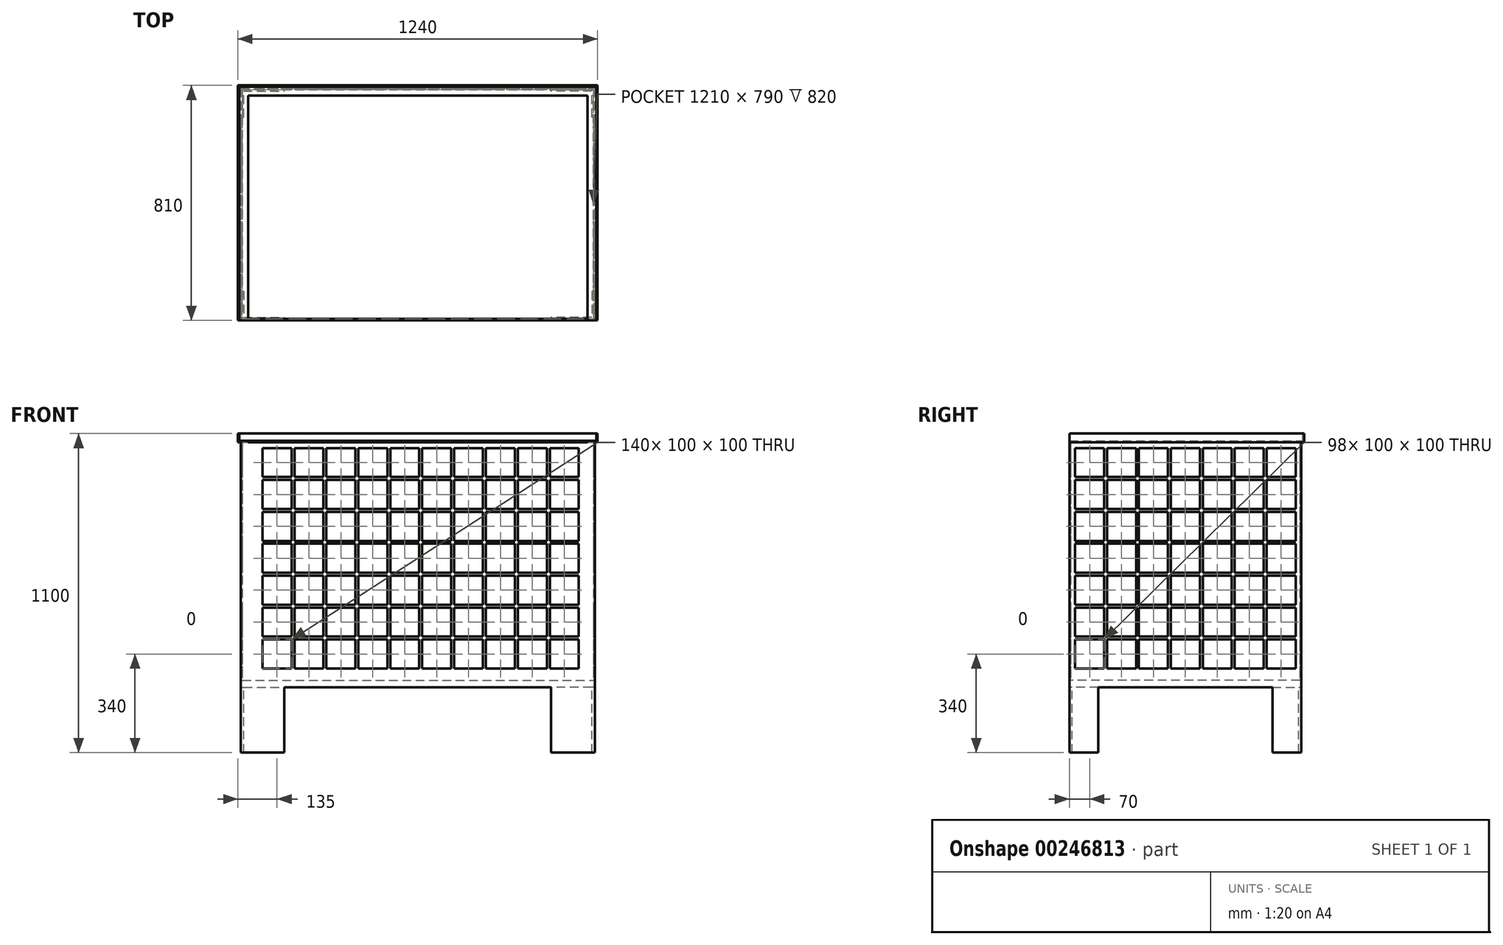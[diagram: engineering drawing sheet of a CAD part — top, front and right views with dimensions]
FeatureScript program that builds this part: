
annotation { "Feature Type Name" : "Feature", "Feature Type Description" : "" }
export const myFeature = defineFeature(function(context is Context, id is Id, definition is map)
    precondition{}
    {
        {
            var Q0;
            Q0=qCreatedBy(makeId("Top.planeOp"),FACE);
            var sketch = newSketch(context, id + "F0", { "sketchPlane" : qUnion([Q0])});
            skLineSegment(sketch, "E0.bottom", {"start": v(-610, 400) * mm, "end": v(610, 400) * mm});
            skLineSegment(sketch, "E0.top", {"start": v(-610, -400) * mm, "end": v(610, -400) * mm});
            skLineSegment(sketch, "E0.left", {"start": v(-610, 400) * mm, "end": v(-610, -400) * mm});
            skLineSegment(sketch, "E0.right", {"start": v(610, 400) * mm, "end": v(610, -400) * mm});
            skPoint(sketch, "E0.middle", {"position": v(0, 0) * mm});
            skSolve(sketch);
        }
        {
            var Q0;
            Q0=makeQuery(id+"F0.imprint","IMPRINT",FACE,{"disambiguationData":[TD([[makeQuery(id+"F0.imprint","IMPRINT",EDGE,{"derivedFrom":sQuery(id+"F0.wireOp",EDGE,"E0.bottom")}),-1.0]])]});
            extrude(context, id + "F1", {"entities" : qUnion([Q0]), "depth" : 25 * mm});
        }
        {
            var Q0;
            Q0=makeQuery(id+"F1.opExtrude","CAP_FACE",FACE,{"disambiguationData":[OSD([sQuery(id+"F0.wireOp",EDGE,"E0.bottom"),sQuery(id+"F0.wireOp",EDGE,"E0.top"),sQuery(id+"F0.wireOp",EDGE,"E0.left"),sQuery(id+"F0.wireOp",EDGE,"E0.right")])],"isStart":true});
            var sketch = newSketch(context, id + "F2", { "sketchPlane" : qUnion([Q0])});
            skLineSegment(sketch, "E1", {"start": v(-610, 400) * mm, "end": v(-610, 300) * mm});
            skLineSegment(sketch, "E2", {"start": v(-610, 300) * mm, "end": v(-600, 300) * mm});
            skLineSegment(sketch, "E3", {"start": v(-600, 300) * mm, "end": v(-600, 390) * mm});
            skLineSegment(sketch, "E4", {"start": v(-600, 390) * mm, "end": v(-460, 390) * mm});
            skLineSegment(sketch, "E5", {"start": v(-460, 390) * mm, "end": v(-460, 400) * mm});
            skLineSegment(sketch, "E6", {"start": v(-460, 400) * mm, "end": v(-610, 400) * mm});
            skLineSegment(sketch, "E7.MirrorCS", {"start": v(460, 390) * mm, "end": v(460, 400) * mm});
            skLineSegment(sketch, "E8.MirrorCS", {"start": v(610, 300) * mm, "end": v(600, 300) * mm});
            skLineSegment(sketch, "E9.MirrorCS", {"start": v(460, 400) * mm, "end": v(610, 400) * mm});
            skLineSegment(sketch, "E10.MirrorCS", {"start": v(600, 390) * mm, "end": v(460, 390) * mm});
            skLineSegment(sketch, "E11.MirrorCS", {"start": v(600, 300) * mm, "end": v(600, 390) * mm});
            skLineSegment(sketch, "E12.MirrorCS", {"start": v(610, 400) * mm, "end": v(610, 300) * mm});
            skLineSegment(sketch, "E13.MirrorCS", {"start": v(-610, -300) * mm, "end": v(-600, -300) * mm});
            skLineSegment(sketch, "E14.MirrorCS", {"start": v(460, -390) * mm, "end": v(460, -400) * mm});
            skLineSegment(sketch, "E15.MirrorCS", {"start": v(610, -300) * mm, "end": v(600, -300) * mm});
            skLineSegment(sketch, "E16.MirrorCS", {"start": v(-460, -390) * mm, "end": v(-460, -400) * mm});
            skLineSegment(sketch, "E17.MirrorCS", {"start": v(460, -400) * mm, "end": v(610, -400) * mm});
            skLineSegment(sketch, "E18.MirrorCS", {"start": v(600, -390) * mm, "end": v(460, -390) * mm});
            skLineSegment(sketch, "E19.MirrorCS", {"start": v(600, -300) * mm, "end": v(600, -390) * mm});
            skLineSegment(sketch, "E20.MirrorCS", {"start": v(610, -400) * mm, "end": v(610, -300) * mm});
            skLineSegment(sketch, "E21.MirrorCS", {"start": v(-460, -400) * mm, "end": v(-610, -400) * mm});
            skLineSegment(sketch, "E22.MirrorCS", {"start": v(-600, -300) * mm, "end": v(-600, -390) * mm});
            skLineSegment(sketch, "E23.MirrorCS", {"start": v(-600, -390) * mm, "end": v(-460, -390) * mm});
            skLineSegment(sketch, "E24.MirrorCS", {"start": v(-610, -400) * mm, "end": v(-610, -300) * mm});
            skSolve(sketch);
        }
        {
            var Q0;
            Q0 = qSketchRegion(id + "F2", true);
            extrude(context, id + "F3", {"entities" : qUnion([Q0]), "operationType" : NewBodyOperationType.ADD, "depth" : 225 * mm});
        }
        {
            var Q0;
            Q0=makeQuery(id+"F1.opExtrude","CAP_FACE",FACE,{"disambiguationData":[OSD([sQuery(id+"F0.wireOp",EDGE,"E0.bottom"),sQuery(id+"F0.wireOp",EDGE,"E0.top"),sQuery(id+"F0.wireOp",EDGE,"E0.left"),sQuery(id+"F0.wireOp",EDGE,"E0.right")])],"isStart":false});
            var sketch = newSketch(context, id + "F4", { "sketchPlane" : qUnion([Q0])});
            skLineSegment(sketch, "E25.0", {"start": v(-610, 400) * mm, "end": v(-610, -400) * mm});
            skLineSegment(sketch, "E26.0", {"start": v(-610, 400) * mm, "end": v(610, 400) * mm});
            skLineSegment(sketch, "E27.0", {"start": v(610, 400) * mm, "end": v(610, -400) * mm});
            skLineSegment(sketch, "E28.0", {"start": v(-610, -400) * mm, "end": v(610, -400) * mm});
            skLineSegment(sketch, "E29.0", {"start": v(-605, 395) * mm, "end": v(-605, -395) * mm});
            skLineSegment(sketch, "E29.1", {"start": v(-605, 395) * mm, "end": v(605, 395) * mm});
            skLineSegment(sketch, "E29.2", {"start": v(605, 395) * mm, "end": v(605, -395) * mm});
            skLineSegment(sketch, "E29.3", {"start": v(-605, -395) * mm, "end": v(605, -395) * mm});
            skSolve(sketch);
        }
        {
            var Q0;
            Q0 = qSketchRegion(id + "F4", true);
            extrude(context, id + "F5", {"entities" : qUnion([Q0]), "operationType" : NewBodyOperationType.ADD, "depth" : 820 * mm});
        }
        {
            var Q0;
            Q0=makeQuery(id+"F5.boolean.opBoolean","MERGE",FACE,{"derivedFrom":[makeQuery(id+"F3.boolean.opBoolean","MERGE",FACE,{"derivedFrom":[makeQuery(id+"F1.opExtrude","SWEPT_FACE",FACE,{"disambiguationData":[OSD([sQuery(id+"F0.wireOp",EDGE,"E0.top")])]}),makeQuery(id+"F3.opExtrude","SWEPT_FACE",FACE,{"disambiguationData":[OSD([sQuery(id+"F2.wireOp",EDGE,"E9.MirrorCS")])]}),makeQuery(id+"F3.opExtrude","SWEPT_FACE",FACE,{"disambiguationData":[OSD([sQuery(id+"F2.wireOp",EDGE,"E6")])]})]}),makeQuery(id+"F5.opExtrude","SWEPT_FACE",FACE,{"disambiguationData":[OSD([sQuery(id+"F4.wireOp",EDGE,"E28.0")])]})]});
            var sketch = newSketch(context, id + "F6", { "sketchPlane" : qUnion([Q0])});
            skLineSegment(sketch, "E30", {"start": v(-585, 845) * mm, "end": v(-620, 845) * mm});
            skLineSegment(sketch, "E31", {"start": v(-620, 845) * mm, "end": v(-620, 875) * mm});
            skLineSegment(sketch, "E32", {"start": v(-620, 875) * mm, "end": v(-615, 875) * mm});
            skLineSegment(sketch, "E33", {"start": v(-615, 875) * mm, "end": v(-615, 850) * mm});
            skLineSegment(sketch, "E34", {"start": v(-615, 850) * mm, "end": v(-585, 850) * mm});
            skLineSegment(sketch, "E35", {"start": v(-585, 850) * mm, "end": v(-585, 845) * mm});
            skSolve(sketch);
        }
        {
            var Q0;
            Q0=makeQuery(id+"F5.opExtrude","CAP_FACE",FACE,{"disambiguationData":[OSD([sQuery(id+"F4.wireOp",EDGE,"E25.0"),sQuery(id+"F4.wireOp",EDGE,"E26.0"),sQuery(id+"F4.wireOp",EDGE,"E27.0"),sQuery(id+"F4.wireOp",EDGE,"E28.0"),sQuery(id+"F4.wireOp",EDGE,"E29.0"),sQuery(id+"F4.wireOp",EDGE,"E29.1"),sQuery(id+"F4.wireOp",EDGE,"E29.2"),sQuery(id+"F4.wireOp",EDGE,"E29.3")])],"isStart":false});
            var sketch = newSketch(context, id + "F7", { "sketchPlane" : qUnion([Q0])});
            skLineSegment(sketch, "E36.0", {"start": v(-610, 400) * mm, "end": v(-610, -400) * mm});
            skLineSegment(sketch, "E37.0", {"start": v(-610, 400) * mm, "end": v(610, 400) * mm});
            skLineSegment(sketch, "E38.0", {"start": v(610, 400) * mm, "end": v(610, -400) * mm});
            skSolve(sketch);
        }
        {
            var Q0;
            {var subQ0=sQuery(id+"F6.wireOp",EDGE,"E31");Q0=makeQuery(id+"F6.imprint","IMPRINT",FACE,{"disambiguationData":[TD([[makeQuery(id+"F6.imprint","IMPRINT",EDGE,{"derivedFrom":subQ0}),-1.0]])]});}
            var Q1;
            Q1 = qConstructionFilter(qBodyType(qCreatedBy(id + "F7" ,EDGE), BodyType.WIRE), ConstructionObject.NO);
            sweep(context, id + "F8", {"operationType" : NewBodyOperationType.ADD, "profiles" : qUnion([Q0]), "path" : qUnion([Q1])});
        }
        {
            var Q0;
            Q0=makeQuery(id+"F5.boolean.opBoolean","MERGE",FACE,{"derivedFrom":[makeQuery(id+"F3.boolean.opBoolean","MERGE",FACE,{"derivedFrom":[makeQuery(id+"F1.opExtrude","SWEPT_FACE",FACE,{"disambiguationData":[OSD([sQuery(id+"F0.wireOp",EDGE,"E0.right")])]}),makeQuery(id+"F3.opExtrude","SWEPT_FACE",FACE,{"disambiguationData":[OSD([sQuery(id+"F2.wireOp",EDGE,"E12.MirrorCS")])]}),makeQuery(id+"F3.opExtrude","SWEPT_FACE",FACE,{"disambiguationData":[OSD([sQuery(id+"F2.wireOp",EDGE,"E20.MirrorCS")])]})]}),makeQuery(id+"F5.opExtrude","SWEPT_FACE",FACE,{"disambiguationData":[OSD([sQuery(id+"F4.wireOp",EDGE,"E27.0")])]})]});
            var sketch = newSketch(context, id + "F9", { "sketchPlane" : qUnion([Q0])});
            skLineSegment(sketch, "E39.bottom", {"start": v(-380, 825) * mm, "end": v(-280, 825) * mm});
            skLineSegment(sketch, "E39.top", {"start": v(-380, 725) * mm, "end": v(-280, 725) * mm});
            skLineSegment(sketch, "E39.left", {"start": v(-380, 825) * mm, "end": v(-380, 725) * mm});
            skLineSegment(sketch, "E39.right", {"start": v(-280, 825) * mm, "end": v(-280, 725) * mm});
            skLineSegment(sketch, "E40.0.1.0", {"start": v(-380, 715) * mm, "end": v(-280, 715) * mm});
            skLineSegment(sketch, "E40.0.1.1", {"start": v(-380, 715) * mm, "end": v(-380, 615) * mm});
            skLineSegment(sketch, "E40.0.1.2", {"start": v(-280, 715) * mm, "end": v(-280, 615) * mm});
            skLineSegment(sketch, "E40.0.1.3", {"start": v(-380, 615) * mm, "end": v(-280, 615) * mm});
            skLineSegment(sketch, "E40.0.2.0", {"start": v(-380, 605) * mm, "end": v(-280, 605) * mm});
            skLineSegment(sketch, "E40.0.2.1", {"start": v(-380, 605) * mm, "end": v(-380, 505) * mm});
            skLineSegment(sketch, "E40.0.2.2", {"start": v(-280, 605) * mm, "end": v(-280, 505) * mm});
            skLineSegment(sketch, "E40.0.2.3", {"start": v(-380, 505) * mm, "end": v(-280, 505) * mm});
            skLineSegment(sketch, "E40.0.3.0", {"start": v(-380, 495) * mm, "end": v(-280, 495) * mm});
            skLineSegment(sketch, "E40.0.3.1", {"start": v(-380, 495) * mm, "end": v(-380, 395) * mm});
            skLineSegment(sketch, "E40.0.3.2", {"start": v(-280, 495) * mm, "end": v(-280, 395) * mm});
            skLineSegment(sketch, "E40.0.3.3", {"start": v(-380, 395) * mm, "end": v(-280, 395) * mm});
            skLineSegment(sketch, "E40.0.4.0", {"start": v(-380, 385) * mm, "end": v(-280, 385) * mm});
            skLineSegment(sketch, "E40.0.4.1", {"start": v(-380, 385) * mm, "end": v(-380, 285) * mm});
            skLineSegment(sketch, "E40.0.4.2", {"start": v(-280, 385) * mm, "end": v(-280, 285) * mm});
            skLineSegment(sketch, "E40.0.4.3", {"start": v(-380, 285) * mm, "end": v(-280, 285) * mm});
            skLineSegment(sketch, "E40.0.5.0", {"start": v(-380, 275) * mm, "end": v(-280, 275) * mm});
            skLineSegment(sketch, "E40.0.5.1", {"start": v(-380, 275) * mm, "end": v(-380, 175) * mm});
            skLineSegment(sketch, "E40.0.5.2", {"start": v(-280, 275) * mm, "end": v(-280, 175) * mm});
            skLineSegment(sketch, "E40.0.5.3", {"start": v(-380, 175) * mm, "end": v(-280, 175) * mm});
            skLineSegment(sketch, "E40.0.6.0", {"start": v(-380, 165) * mm, "end": v(-280, 165) * mm});
            skLineSegment(sketch, "E40.0.6.1", {"start": v(-380, 165) * mm, "end": v(-380, 65) * mm});
            skLineSegment(sketch, "E40.0.6.2", {"start": v(-280, 165) * mm, "end": v(-280, 65) * mm});
            skLineSegment(sketch, "E40.0.6.3", {"start": v(-380, 65) * mm, "end": v(-280, 65) * mm});
            skLineSegment(sketch, "E40.1.0.0", {"start": v(-270, 825) * mm, "end": v(-170, 825) * mm});
            skLineSegment(sketch, "E40.1.0.1", {"start": v(-270, 825) * mm, "end": v(-270, 725) * mm});
            skLineSegment(sketch, "E40.1.0.2", {"start": v(-170, 825) * mm, "end": v(-170, 725) * mm});
            skLineSegment(sketch, "E40.1.0.3", {"start": v(-270, 725) * mm, "end": v(-170, 725) * mm});
            skLineSegment(sketch, "E40.1.1.0", {"start": v(-270, 715) * mm, "end": v(-170, 715) * mm});
            skLineSegment(sketch, "E40.1.1.1", {"start": v(-270, 715) * mm, "end": v(-270, 615) * mm});
            skLineSegment(sketch, "E40.1.1.2", {"start": v(-170, 715) * mm, "end": v(-170, 615) * mm});
            skLineSegment(sketch, "E40.1.1.3", {"start": v(-270, 615) * mm, "end": v(-170, 615) * mm});
            skLineSegment(sketch, "E40.1.2.0", {"start": v(-270, 605) * mm, "end": v(-170, 605) * mm});
            skLineSegment(sketch, "E40.1.2.1", {"start": v(-270, 605) * mm, "end": v(-270, 505) * mm});
            skLineSegment(sketch, "E40.1.2.2", {"start": v(-170, 605) * mm, "end": v(-170, 505) * mm});
            skLineSegment(sketch, "E40.1.2.3", {"start": v(-270, 505) * mm, "end": v(-170, 505) * mm});
            skLineSegment(sketch, "E40.1.3.0", {"start": v(-270, 495) * mm, "end": v(-170, 495) * mm});
            skLineSegment(sketch, "E40.1.3.1", {"start": v(-270, 495) * mm, "end": v(-270, 395) * mm});
            skLineSegment(sketch, "E40.1.3.2", {"start": v(-170, 495) * mm, "end": v(-170, 395) * mm});
            skLineSegment(sketch, "E40.1.3.3", {"start": v(-270, 395) * mm, "end": v(-170, 395) * mm});
            skLineSegment(sketch, "E40.1.4.0", {"start": v(-270, 385) * mm, "end": v(-170, 385) * mm});
            skLineSegment(sketch, "E40.1.4.1", {"start": v(-270, 385) * mm, "end": v(-270, 285) * mm});
            skLineSegment(sketch, "E40.1.4.2", {"start": v(-170, 385) * mm, "end": v(-170, 285) * mm});
            skLineSegment(sketch, "E40.1.4.3", {"start": v(-270, 285) * mm, "end": v(-170, 285) * mm});
            skLineSegment(sketch, "E40.1.5.0", {"start": v(-270, 275) * mm, "end": v(-170, 275) * mm});
            skLineSegment(sketch, "E40.1.5.1", {"start": v(-270, 275) * mm, "end": v(-270, 175) * mm});
            skLineSegment(sketch, "E40.1.5.2", {"start": v(-170, 275) * mm, "end": v(-170, 175) * mm});
            skLineSegment(sketch, "E40.1.5.3", {"start": v(-270, 175) * mm, "end": v(-170, 175) * mm});
            skLineSegment(sketch, "E40.1.6.0", {"start": v(-270, 165) * mm, "end": v(-170, 165) * mm});
            skLineSegment(sketch, "E40.1.6.1", {"start": v(-270, 165) * mm, "end": v(-270, 65) * mm});
            skLineSegment(sketch, "E40.1.6.2", {"start": v(-170, 165) * mm, "end": v(-170, 65) * mm});
            skLineSegment(sketch, "E40.1.6.3", {"start": v(-270, 65) * mm, "end": v(-170, 65) * mm});
            skLineSegment(sketch, "E40.2.0.0", {"start": v(-160, 825) * mm, "end": v(-60, 825) * mm});
            skLineSegment(sketch, "E40.2.0.1", {"start": v(-160, 825) * mm, "end": v(-160, 725) * mm});
            skLineSegment(sketch, "E40.2.0.2", {"start": v(-60, 825) * mm, "end": v(-60, 725) * mm});
            skLineSegment(sketch, "E40.2.0.3", {"start": v(-160, 725) * mm, "end": v(-60, 725) * mm});
            skLineSegment(sketch, "E40.2.1.0", {"start": v(-160, 715) * mm, "end": v(-60, 715) * mm});
            skLineSegment(sketch, "E40.2.1.1", {"start": v(-160, 715) * mm, "end": v(-160, 615) * mm});
            skLineSegment(sketch, "E40.2.1.2", {"start": v(-60, 715) * mm, "end": v(-60, 615) * mm});
            skLineSegment(sketch, "E40.2.1.3", {"start": v(-160, 615) * mm, "end": v(-60, 615) * mm});
            skLineSegment(sketch, "E40.2.2.0", {"start": v(-160, 605) * mm, "end": v(-60, 605) * mm});
            skLineSegment(sketch, "E40.2.2.1", {"start": v(-160, 605) * mm, "end": v(-160, 505) * mm});
            skLineSegment(sketch, "E40.2.2.2", {"start": v(-60, 605) * mm, "end": v(-60, 505) * mm});
            skLineSegment(sketch, "E40.2.2.3", {"start": v(-160, 505) * mm, "end": v(-60, 505) * mm});
            skLineSegment(sketch, "E40.2.3.0", {"start": v(-160, 495) * mm, "end": v(-60, 495) * mm});
            skLineSegment(sketch, "E40.2.3.1", {"start": v(-160, 495) * mm, "end": v(-160, 395) * mm});
            skLineSegment(sketch, "E40.2.3.2", {"start": v(-60, 495) * mm, "end": v(-60, 395) * mm});
            skLineSegment(sketch, "E40.2.3.3", {"start": v(-160, 395) * mm, "end": v(-60, 395) * mm});
            skLineSegment(sketch, "E40.2.4.0", {"start": v(-160, 385) * mm, "end": v(-60, 385) * mm});
            skLineSegment(sketch, "E40.2.4.1", {"start": v(-160, 385) * mm, "end": v(-160, 285) * mm});
            skLineSegment(sketch, "E40.2.4.2", {"start": v(-60, 385) * mm, "end": v(-60, 285) * mm});
            skLineSegment(sketch, "E40.2.4.3", {"start": v(-160, 285) * mm, "end": v(-60, 285) * mm});
            skLineSegment(sketch, "E40.2.5.0", {"start": v(-160, 275) * mm, "end": v(-60, 275) * mm});
            skLineSegment(sketch, "E40.2.5.1", {"start": v(-160, 275) * mm, "end": v(-160, 175) * mm});
            skLineSegment(sketch, "E40.2.5.2", {"start": v(-60, 275) * mm, "end": v(-60, 175) * mm});
            skLineSegment(sketch, "E40.2.5.3", {"start": v(-160, 175) * mm, "end": v(-60, 175) * mm});
            skLineSegment(sketch, "E40.2.6.0", {"start": v(-160, 165) * mm, "end": v(-60, 165) * mm});
            skLineSegment(sketch, "E40.2.6.1", {"start": v(-160, 165) * mm, "end": v(-160, 65) * mm});
            skLineSegment(sketch, "E40.2.6.2", {"start": v(-60, 165) * mm, "end": v(-60, 65) * mm});
            skLineSegment(sketch, "E40.2.6.3", {"start": v(-160, 65) * mm, "end": v(-60, 65) * mm});
            skLineSegment(sketch, "E40.3.0.0", {"start": v(-50, 825) * mm, "end": v(50, 825) * mm});
            skLineSegment(sketch, "E40.3.0.1", {"start": v(-50, 825) * mm, "end": v(-50, 725) * mm});
            skLineSegment(sketch, "E40.3.0.2", {"start": v(50, 825) * mm, "end": v(50, 725) * mm});
            skLineSegment(sketch, "E40.3.0.3", {"start": v(-50, 725) * mm, "end": v(50, 725) * mm});
            skLineSegment(sketch, "E40.3.1.0", {"start": v(-50, 715) * mm, "end": v(50, 715) * mm});
            skLineSegment(sketch, "E40.3.1.1", {"start": v(-50, 715) * mm, "end": v(-50, 615) * mm});
            skLineSegment(sketch, "E40.3.1.2", {"start": v(50, 715) * mm, "end": v(50, 615) * mm});
            skLineSegment(sketch, "E40.3.1.3", {"start": v(-50, 615) * mm, "end": v(50, 615) * mm});
            skLineSegment(sketch, "E40.3.2.0", {"start": v(-50, 605) * mm, "end": v(50, 605) * mm});
            skLineSegment(sketch, "E40.3.2.1", {"start": v(-50, 605) * mm, "end": v(-50, 505) * mm});
            skLineSegment(sketch, "E40.3.2.2", {"start": v(50, 605) * mm, "end": v(50, 505) * mm});
            skLineSegment(sketch, "E40.3.2.3", {"start": v(-50, 505) * mm, "end": v(50, 505) * mm});
            skLineSegment(sketch, "E40.3.3.0", {"start": v(-50, 495) * mm, "end": v(50, 495) * mm});
            skLineSegment(sketch, "E40.3.3.1", {"start": v(-50, 495) * mm, "end": v(-50, 395) * mm});
            skLineSegment(sketch, "E40.3.3.2", {"start": v(50, 495) * mm, "end": v(50, 395) * mm});
            skLineSegment(sketch, "E40.3.3.3", {"start": v(-50, 395) * mm, "end": v(50, 395) * mm});
            skLineSegment(sketch, "E40.3.4.0", {"start": v(-50, 385) * mm, "end": v(50, 385) * mm});
            skLineSegment(sketch, "E40.3.4.1", {"start": v(-50, 385) * mm, "end": v(-50, 285) * mm});
            skLineSegment(sketch, "E40.3.4.2", {"start": v(50, 385) * mm, "end": v(50, 285) * mm});
            skLineSegment(sketch, "E40.3.4.3", {"start": v(-50, 285) * mm, "end": v(50, 285) * mm});
            skLineSegment(sketch, "E40.3.5.0", {"start": v(-50, 275) * mm, "end": v(50, 275) * mm});
            skLineSegment(sketch, "E40.3.5.1", {"start": v(-50, 275) * mm, "end": v(-50, 175) * mm});
            skLineSegment(sketch, "E40.3.5.2", {"start": v(50, 275) * mm, "end": v(50, 175) * mm});
            skLineSegment(sketch, "E40.3.5.3", {"start": v(-50, 175) * mm, "end": v(50, 175) * mm});
            skLineSegment(sketch, "E40.3.6.0", {"start": v(-50, 165) * mm, "end": v(50, 165) * mm});
            skLineSegment(sketch, "E40.3.6.1", {"start": v(-50, 165) * mm, "end": v(-50, 65) * mm});
            skLineSegment(sketch, "E40.3.6.2", {"start": v(50, 165) * mm, "end": v(50, 65) * mm});
            skLineSegment(sketch, "E40.3.6.3", {"start": v(-50, 65) * mm, "end": v(50, 65) * mm});
            skLineSegment(sketch, "E40.4.0.0", {"start": v(60, 825) * mm, "end": v(160, 825) * mm});
            skLineSegment(sketch, "E40.4.0.1", {"start": v(60, 825) * mm, "end": v(60, 725) * mm});
            skLineSegment(sketch, "E40.4.0.2", {"start": v(160, 825) * mm, "end": v(160, 725) * mm});
            skLineSegment(sketch, "E40.4.0.3", {"start": v(60, 725) * mm, "end": v(160, 725) * mm});
            skLineSegment(sketch, "E40.4.1.0", {"start": v(60, 715) * mm, "end": v(160, 715) * mm});
            skLineSegment(sketch, "E40.4.1.1", {"start": v(60, 715) * mm, "end": v(60, 615) * mm});
            skLineSegment(sketch, "E40.4.1.2", {"start": v(160, 715) * mm, "end": v(160, 615) * mm});
            skLineSegment(sketch, "E40.4.1.3", {"start": v(60, 615) * mm, "end": v(160, 615) * mm});
            skLineSegment(sketch, "E40.4.2.0", {"start": v(60, 605) * mm, "end": v(160, 605) * mm});
            skLineSegment(sketch, "E40.4.2.1", {"start": v(60, 605) * mm, "end": v(60, 505) * mm});
            skLineSegment(sketch, "E40.4.2.2", {"start": v(160, 605) * mm, "end": v(160, 505) * mm});
            skLineSegment(sketch, "E40.4.2.3", {"start": v(60, 505) * mm, "end": v(160, 505) * mm});
            skLineSegment(sketch, "E40.4.3.0", {"start": v(60, 495) * mm, "end": v(160, 495) * mm});
            skLineSegment(sketch, "E40.4.3.1", {"start": v(60, 495) * mm, "end": v(60, 395) * mm});
            skLineSegment(sketch, "E40.4.3.2", {"start": v(160, 495) * mm, "end": v(160, 395) * mm});
            skLineSegment(sketch, "E40.4.3.3", {"start": v(60, 395) * mm, "end": v(160, 395) * mm});
            skLineSegment(sketch, "E40.4.4.0", {"start": v(60, 385) * mm, "end": v(160, 385) * mm});
            skLineSegment(sketch, "E40.4.4.1", {"start": v(60, 385) * mm, "end": v(60, 285) * mm});
            skLineSegment(sketch, "E40.4.4.2", {"start": v(160, 385) * mm, "end": v(160, 285) * mm});
            skLineSegment(sketch, "E40.4.4.3", {"start": v(60, 285) * mm, "end": v(160, 285) * mm});
            skLineSegment(sketch, "E40.4.5.0", {"start": v(60, 275) * mm, "end": v(160, 275) * mm});
            skLineSegment(sketch, "E40.4.5.1", {"start": v(60, 275) * mm, "end": v(60, 175) * mm});
            skLineSegment(sketch, "E40.4.5.2", {"start": v(160, 275) * mm, "end": v(160, 175) * mm});
            skLineSegment(sketch, "E40.4.5.3", {"start": v(60, 175) * mm, "end": v(160, 175) * mm});
            skLineSegment(sketch, "E40.4.6.0", {"start": v(60, 165) * mm, "end": v(160, 165) * mm});
            skLineSegment(sketch, "E40.4.6.1", {"start": v(60, 165) * mm, "end": v(60, 65) * mm});
            skLineSegment(sketch, "E40.4.6.2", {"start": v(160, 165) * mm, "end": v(160, 65) * mm});
            skLineSegment(sketch, "E40.4.6.3", {"start": v(60, 65) * mm, "end": v(160, 65) * mm});
            skLineSegment(sketch, "E40.5.0.0", {"start": v(170, 825) * mm, "end": v(270, 825) * mm});
            skLineSegment(sketch, "E40.5.0.1", {"start": v(170, 825) * mm, "end": v(170, 725) * mm});
            skLineSegment(sketch, "E40.5.0.2", {"start": v(270, 825) * mm, "end": v(270, 725) * mm});
            skLineSegment(sketch, "E40.5.0.3", {"start": v(170, 725) * mm, "end": v(270, 725) * mm});
            skLineSegment(sketch, "E40.5.1.0", {"start": v(170, 715) * mm, "end": v(270, 715) * mm});
            skLineSegment(sketch, "E40.5.1.1", {"start": v(170, 715) * mm, "end": v(170, 615) * mm});
            skLineSegment(sketch, "E40.5.1.2", {"start": v(270, 715) * mm, "end": v(270, 615) * mm});
            skLineSegment(sketch, "E40.5.1.3", {"start": v(170, 615) * mm, "end": v(270, 615) * mm});
            skLineSegment(sketch, "E40.5.2.0", {"start": v(170, 605) * mm, "end": v(270, 605) * mm});
            skLineSegment(sketch, "E40.5.2.1", {"start": v(170, 605) * mm, "end": v(170, 505) * mm});
            skLineSegment(sketch, "E40.5.2.2", {"start": v(270, 605) * mm, "end": v(270, 505) * mm});
            skLineSegment(sketch, "E40.5.2.3", {"start": v(170, 505) * mm, "end": v(270, 505) * mm});
            skLineSegment(sketch, "E40.5.3.0", {"start": v(170, 495) * mm, "end": v(270, 495) * mm});
            skLineSegment(sketch, "E40.5.3.1", {"start": v(170, 495) * mm, "end": v(170, 395) * mm});
            skLineSegment(sketch, "E40.5.3.2", {"start": v(270, 495) * mm, "end": v(270, 395) * mm});
            skLineSegment(sketch, "E40.5.3.3", {"start": v(170, 395) * mm, "end": v(270, 395) * mm});
            skLineSegment(sketch, "E40.5.4.0", {"start": v(170, 385) * mm, "end": v(270, 385) * mm});
            skLineSegment(sketch, "E40.5.4.1", {"start": v(170, 385) * mm, "end": v(170, 285) * mm});
            skLineSegment(sketch, "E40.5.4.2", {"start": v(270, 385) * mm, "end": v(270, 285) * mm});
            skLineSegment(sketch, "E40.5.4.3", {"start": v(170, 285) * mm, "end": v(270, 285) * mm});
            skLineSegment(sketch, "E40.5.5.0", {"start": v(170, 275) * mm, "end": v(270, 275) * mm});
            skLineSegment(sketch, "E40.5.5.1", {"start": v(170, 275) * mm, "end": v(170, 175) * mm});
            skLineSegment(sketch, "E40.5.5.2", {"start": v(270, 275) * mm, "end": v(270, 175) * mm});
            skLineSegment(sketch, "E40.5.5.3", {"start": v(170, 175) * mm, "end": v(270, 175) * mm});
            skLineSegment(sketch, "E40.5.6.0", {"start": v(170, 165) * mm, "end": v(270, 165) * mm});
            skLineSegment(sketch, "E40.5.6.1", {"start": v(170, 165) * mm, "end": v(170, 65) * mm});
            skLineSegment(sketch, "E40.5.6.2", {"start": v(270, 165) * mm, "end": v(270, 65) * mm});
            skLineSegment(sketch, "E40.5.6.3", {"start": v(170, 65) * mm, "end": v(270, 65) * mm});
            skLineSegment(sketch, "E40.6.0.0", {"start": v(280, 825) * mm, "end": v(380, 825) * mm});
            skLineSegment(sketch, "E40.6.0.1", {"start": v(280, 825) * mm, "end": v(280, 725) * mm});
            skLineSegment(sketch, "E40.6.0.2", {"start": v(380, 825) * mm, "end": v(380, 725) * mm});
            skLineSegment(sketch, "E40.6.0.3", {"start": v(280, 725) * mm, "end": v(380, 725) * mm});
            skLineSegment(sketch, "E40.6.1.0", {"start": v(280, 715) * mm, "end": v(380, 715) * mm});
            skLineSegment(sketch, "E40.6.1.1", {"start": v(280, 715) * mm, "end": v(280, 615) * mm});
            skLineSegment(sketch, "E40.6.1.2", {"start": v(380, 715) * mm, "end": v(380, 615) * mm});
            skLineSegment(sketch, "E40.6.1.3", {"start": v(280, 615) * mm, "end": v(380, 615) * mm});
            skLineSegment(sketch, "E40.6.2.0", {"start": v(280, 605) * mm, "end": v(380, 605) * mm});
            skLineSegment(sketch, "E40.6.2.1", {"start": v(280, 605) * mm, "end": v(280, 505) * mm});
            skLineSegment(sketch, "E40.6.2.2", {"start": v(380, 605) * mm, "end": v(380, 505) * mm});
            skLineSegment(sketch, "E40.6.2.3", {"start": v(280, 505) * mm, "end": v(380, 505) * mm});
            skLineSegment(sketch, "E40.6.3.0", {"start": v(280, 495) * mm, "end": v(380, 495) * mm});
            skLineSegment(sketch, "E40.6.3.1", {"start": v(280, 495) * mm, "end": v(280, 395) * mm});
            skLineSegment(sketch, "E40.6.3.2", {"start": v(380, 495) * mm, "end": v(380, 395) * mm});
            skLineSegment(sketch, "E40.6.3.3", {"start": v(280, 395) * mm, "end": v(380, 395) * mm});
            skLineSegment(sketch, "E40.6.4.0", {"start": v(280, 385) * mm, "end": v(380, 385) * mm});
            skLineSegment(sketch, "E40.6.4.1", {"start": v(280, 385) * mm, "end": v(280, 285) * mm});
            skLineSegment(sketch, "E40.6.4.2", {"start": v(380, 385) * mm, "end": v(380, 285) * mm});
            skLineSegment(sketch, "E40.6.4.3", {"start": v(280, 285) * mm, "end": v(380, 285) * mm});
            skLineSegment(sketch, "E40.6.5.0", {"start": v(280, 275) * mm, "end": v(380, 275) * mm});
            skLineSegment(sketch, "E40.6.5.1", {"start": v(280, 275) * mm, "end": v(280, 175) * mm});
            skLineSegment(sketch, "E40.6.5.2", {"start": v(380, 275) * mm, "end": v(380, 175) * mm});
            skLineSegment(sketch, "E40.6.5.3", {"start": v(280, 175) * mm, "end": v(380, 175) * mm});
            skLineSegment(sketch, "E40.6.6.0", {"start": v(280, 165) * mm, "end": v(380, 165) * mm});
            skLineSegment(sketch, "E40.6.6.1", {"start": v(280, 165) * mm, "end": v(280, 65) * mm});
            skLineSegment(sketch, "E40.6.6.2", {"start": v(380, 165) * mm, "end": v(380, 65) * mm});
            skLineSegment(sketch, "E40.6.6.3", {"start": v(280, 65) * mm, "end": v(380, 65) * mm});
            skLineSegment(sketch, "E40.direction1", {"start": v(-380, 825) * mm, "end": v(-270, 825) * mm, "construction": true});
            skLineSegment(sketch, "E40.direction2", {"start": v(-380, 825) * mm, "end": v(-380, 715) * mm, "construction": true});
            skSolve(sketch);
        }
        {
            var Q0;
            Q0 = qSketchRegion(id + "F9", true);
            extrude(context, id + "F10", {"entities" : qUnion([Q0]), "operationType" : NewBodyOperationType.REMOVE, "endBound" : BoundingType.THROUGH_ALL, "oppositeDirection" : true, "depth" : 25 * mm});
        }
        {
            var Q0;
            Q0=makeQuery(id+"F5.boolean.opBoolean","MERGE",FACE,{"derivedFrom":[makeQuery(id+"F3.boolean.opBoolean","MERGE",FACE,{"derivedFrom":[makeQuery(id+"F1.opExtrude","SWEPT_FACE",FACE,{"disambiguationData":[OSD([sQuery(id+"F0.wireOp",EDGE,"E0.bottom")])]}),makeQuery(id+"F3.opExtrude","SWEPT_FACE",FACE,{"disambiguationData":[OSD([sQuery(id+"F2.wireOp",EDGE,"E21.MirrorCS")])]}),makeQuery(id+"F3.opExtrude","SWEPT_FACE",FACE,{"disambiguationData":[OSD([sQuery(id+"F2.wireOp",EDGE,"E17.MirrorCS")])]})]}),makeQuery(id+"F5.opExtrude","SWEPT_FACE",FACE,{"disambiguationData":[OSD([sQuery(id+"F4.wireOp",EDGE,"E26.0")])]})]});
            var sketch = newSketch(context, id + "F11", { "sketchPlane" : qUnion([Q0])});
            skLineSegment(sketch, "E41.bottom", {"start": v(-555, 825) * mm, "end": v(-455, 825) * mm});
            skLineSegment(sketch, "E41.top", {"start": v(-555, 725) * mm, "end": v(-455, 725) * mm});
            skLineSegment(sketch, "E41.left", {"start": v(-555, 825) * mm, "end": v(-555, 725) * mm});
            skLineSegment(sketch, "E41.right", {"start": v(-455, 825) * mm, "end": v(-455, 725) * mm});
            skLineSegment(sketch, "E42.0.1.0", {"start": v(-555, 615) * mm, "end": v(-455, 615) * mm});
            skLineSegment(sketch, "E42.0.1.1", {"start": v(-555, 715) * mm, "end": v(-455, 715) * mm});
            skLineSegment(sketch, "E42.0.1.2", {"start": v(-455, 715) * mm, "end": v(-455, 615) * mm});
            skLineSegment(sketch, "E42.0.1.3", {"start": v(-555, 715) * mm, "end": v(-555, 615) * mm});
            skLineSegment(sketch, "E42.0.2.0", {"start": v(-555, 505) * mm, "end": v(-455, 505) * mm});
            skLineSegment(sketch, "E42.0.2.1", {"start": v(-555, 605) * mm, "end": v(-455, 605) * mm});
            skLineSegment(sketch, "E42.0.2.2", {"start": v(-455, 605) * mm, "end": v(-455, 505) * mm});
            skLineSegment(sketch, "E42.0.2.3", {"start": v(-555, 605) * mm, "end": v(-555, 505) * mm});
            skLineSegment(sketch, "E42.0.3.0", {"start": v(-555, 395) * mm, "end": v(-455, 395) * mm});
            skLineSegment(sketch, "E42.0.3.1", {"start": v(-555, 495) * mm, "end": v(-455, 495) * mm});
            skLineSegment(sketch, "E42.0.3.2", {"start": v(-455, 495) * mm, "end": v(-455, 395) * mm});
            skLineSegment(sketch, "E42.0.3.3", {"start": v(-555, 495) * mm, "end": v(-555, 395) * mm});
            skLineSegment(sketch, "E42.0.4.0", {"start": v(-555, 285) * mm, "end": v(-455, 285) * mm});
            skLineSegment(sketch, "E42.0.4.1", {"start": v(-555, 385) * mm, "end": v(-455, 385) * mm});
            skLineSegment(sketch, "E42.0.4.2", {"start": v(-455, 385) * mm, "end": v(-455, 285) * mm});
            skLineSegment(sketch, "E42.0.4.3", {"start": v(-555, 385) * mm, "end": v(-555, 285) * mm});
            skLineSegment(sketch, "E42.0.5.0", {"start": v(-555, 175) * mm, "end": v(-455, 175) * mm});
            skLineSegment(sketch, "E42.0.5.1", {"start": v(-555, 275) * mm, "end": v(-455, 275) * mm});
            skLineSegment(sketch, "E42.0.5.2", {"start": v(-455, 275) * mm, "end": v(-455, 175) * mm});
            skLineSegment(sketch, "E42.0.5.3", {"start": v(-555, 275) * mm, "end": v(-555, 175) * mm});
            skLineSegment(sketch, "E42.0.6.0", {"start": v(-555, 65) * mm, "end": v(-455, 65) * mm});
            skLineSegment(sketch, "E42.0.6.1", {"start": v(-555, 165) * mm, "end": v(-455, 165) * mm});
            skLineSegment(sketch, "E42.0.6.2", {"start": v(-455, 165) * mm, "end": v(-455, 65) * mm});
            skLineSegment(sketch, "E42.0.6.3", {"start": v(-555, 165) * mm, "end": v(-555, 65) * mm});
            skLineSegment(sketch, "E42.1.0.0", {"start": v(-445, 725) * mm, "end": v(-345, 725) * mm});
            skLineSegment(sketch, "E42.1.0.1", {"start": v(-445, 825) * mm, "end": v(-345, 825) * mm});
            skLineSegment(sketch, "E42.1.0.2", {"start": v(-345, 825) * mm, "end": v(-345, 725) * mm});
            skLineSegment(sketch, "E42.1.0.3", {"start": v(-445, 825) * mm, "end": v(-445, 725) * mm});
            skLineSegment(sketch, "E42.1.1.0", {"start": v(-445, 615) * mm, "end": v(-345, 615) * mm});
            skLineSegment(sketch, "E42.1.1.1", {"start": v(-445, 715) * mm, "end": v(-345, 715) * mm});
            skLineSegment(sketch, "E42.1.1.2", {"start": v(-345, 715) * mm, "end": v(-345, 615) * mm});
            skLineSegment(sketch, "E42.1.1.3", {"start": v(-445, 715) * mm, "end": v(-445, 615) * mm});
            skLineSegment(sketch, "E42.1.2.0", {"start": v(-445, 505) * mm, "end": v(-345, 505) * mm});
            skLineSegment(sketch, "E42.1.2.1", {"start": v(-445, 605) * mm, "end": v(-345, 605) * mm});
            skLineSegment(sketch, "E42.1.2.2", {"start": v(-345, 605) * mm, "end": v(-345, 505) * mm});
            skLineSegment(sketch, "E42.1.2.3", {"start": v(-445, 605) * mm, "end": v(-445, 505) * mm});
            skLineSegment(sketch, "E42.1.3.0", {"start": v(-445, 395) * mm, "end": v(-345, 395) * mm});
            skLineSegment(sketch, "E42.1.3.1", {"start": v(-445, 495) * mm, "end": v(-345, 495) * mm});
            skLineSegment(sketch, "E42.1.3.2", {"start": v(-345, 495) * mm, "end": v(-345, 395) * mm});
            skLineSegment(sketch, "E42.1.3.3", {"start": v(-445, 495) * mm, "end": v(-445, 395) * mm});
            skLineSegment(sketch, "E42.1.4.0", {"start": v(-445, 285) * mm, "end": v(-345, 285) * mm});
            skLineSegment(sketch, "E42.1.4.1", {"start": v(-445, 385) * mm, "end": v(-345, 385) * mm});
            skLineSegment(sketch, "E42.1.4.2", {"start": v(-345, 385) * mm, "end": v(-345, 285) * mm});
            skLineSegment(sketch, "E42.1.4.3", {"start": v(-445, 385) * mm, "end": v(-445, 285) * mm});
            skLineSegment(sketch, "E42.1.5.0", {"start": v(-445, 175) * mm, "end": v(-345, 175) * mm});
            skLineSegment(sketch, "E42.1.5.1", {"start": v(-445, 275) * mm, "end": v(-345, 275) * mm});
            skLineSegment(sketch, "E42.1.5.2", {"start": v(-345, 275) * mm, "end": v(-345, 175) * mm});
            skLineSegment(sketch, "E42.1.5.3", {"start": v(-445, 275) * mm, "end": v(-445, 175) * mm});
            skLineSegment(sketch, "E42.1.6.0", {"start": v(-445, 65) * mm, "end": v(-345, 65) * mm});
            skLineSegment(sketch, "E42.1.6.1", {"start": v(-445, 165) * mm, "end": v(-345, 165) * mm});
            skLineSegment(sketch, "E42.1.6.2", {"start": v(-345, 165) * mm, "end": v(-345, 65) * mm});
            skLineSegment(sketch, "E42.1.6.3", {"start": v(-445, 165) * mm, "end": v(-445, 65) * mm});
            skLineSegment(sketch, "E42.2.0.0", {"start": v(-335, 725) * mm, "end": v(-235, 725) * mm});
            skLineSegment(sketch, "E42.2.0.1", {"start": v(-335, 825) * mm, "end": v(-235, 825) * mm});
            skLineSegment(sketch, "E42.2.0.2", {"start": v(-235, 825) * mm, "end": v(-235, 725) * mm});
            skLineSegment(sketch, "E42.2.0.3", {"start": v(-335, 825) * mm, "end": v(-335, 725) * mm});
            skLineSegment(sketch, "E42.2.1.0", {"start": v(-335, 615) * mm, "end": v(-235, 615) * mm});
            skLineSegment(sketch, "E42.2.1.1", {"start": v(-335, 715) * mm, "end": v(-235, 715) * mm});
            skLineSegment(sketch, "E42.2.1.2", {"start": v(-235, 715) * mm, "end": v(-235, 615) * mm});
            skLineSegment(sketch, "E42.2.1.3", {"start": v(-335, 715) * mm, "end": v(-335, 615) * mm});
            skLineSegment(sketch, "E42.2.2.0", {"start": v(-335, 505) * mm, "end": v(-235, 505) * mm});
            skLineSegment(sketch, "E42.2.2.1", {"start": v(-335, 605) * mm, "end": v(-235, 605) * mm});
            skLineSegment(sketch, "E42.2.2.2", {"start": v(-235, 605) * mm, "end": v(-235, 505) * mm});
            skLineSegment(sketch, "E42.2.2.3", {"start": v(-335, 605) * mm, "end": v(-335, 505) * mm});
            skLineSegment(sketch, "E42.2.3.0", {"start": v(-335, 395) * mm, "end": v(-235, 395) * mm});
            skLineSegment(sketch, "E42.2.3.1", {"start": v(-335, 495) * mm, "end": v(-235, 495) * mm});
            skLineSegment(sketch, "E42.2.3.2", {"start": v(-235, 495) * mm, "end": v(-235, 395) * mm});
            skLineSegment(sketch, "E42.2.3.3", {"start": v(-335, 495) * mm, "end": v(-335, 395) * mm});
            skLineSegment(sketch, "E42.2.4.0", {"start": v(-335, 285) * mm, "end": v(-235, 285) * mm});
            skLineSegment(sketch, "E42.2.4.1", {"start": v(-335, 385) * mm, "end": v(-235, 385) * mm});
            skLineSegment(sketch, "E42.2.4.2", {"start": v(-235, 385) * mm, "end": v(-235, 285) * mm});
            skLineSegment(sketch, "E42.2.4.3", {"start": v(-335, 385) * mm, "end": v(-335, 285) * mm});
            skLineSegment(sketch, "E42.2.5.0", {"start": v(-335, 175) * mm, "end": v(-235, 175) * mm});
            skLineSegment(sketch, "E42.2.5.1", {"start": v(-335, 275) * mm, "end": v(-235, 275) * mm});
            skLineSegment(sketch, "E42.2.5.2", {"start": v(-235, 275) * mm, "end": v(-235, 175) * mm});
            skLineSegment(sketch, "E42.2.5.3", {"start": v(-335, 275) * mm, "end": v(-335, 175) * mm});
            skLineSegment(sketch, "E42.2.6.0", {"start": v(-335, 65) * mm, "end": v(-235, 65) * mm});
            skLineSegment(sketch, "E42.2.6.1", {"start": v(-335, 165) * mm, "end": v(-235, 165) * mm});
            skLineSegment(sketch, "E42.2.6.2", {"start": v(-235, 165) * mm, "end": v(-235, 65) * mm});
            skLineSegment(sketch, "E42.2.6.3", {"start": v(-335, 165) * mm, "end": v(-335, 65) * mm});
            skLineSegment(sketch, "E42.3.0.0", {"start": v(-225, 725) * mm, "end": v(-125, 725) * mm});
            skLineSegment(sketch, "E42.3.0.1", {"start": v(-225, 825) * mm, "end": v(-125, 825) * mm});
            skLineSegment(sketch, "E42.3.0.2", {"start": v(-125, 825) * mm, "end": v(-125, 725) * mm});
            skLineSegment(sketch, "E42.3.0.3", {"start": v(-225, 825) * mm, "end": v(-225, 725) * mm});
            skLineSegment(sketch, "E42.3.1.0", {"start": v(-225, 615) * mm, "end": v(-125, 615) * mm});
            skLineSegment(sketch, "E42.3.1.1", {"start": v(-225, 715) * mm, "end": v(-125, 715) * mm});
            skLineSegment(sketch, "E42.3.1.2", {"start": v(-125, 715) * mm, "end": v(-125, 615) * mm});
            skLineSegment(sketch, "E42.3.1.3", {"start": v(-225, 715) * mm, "end": v(-225, 615) * mm});
            skLineSegment(sketch, "E42.3.2.0", {"start": v(-225, 505) * mm, "end": v(-125, 505) * mm});
            skLineSegment(sketch, "E42.3.2.1", {"start": v(-225, 605) * mm, "end": v(-125, 605) * mm});
            skLineSegment(sketch, "E42.3.2.2", {"start": v(-125, 605) * mm, "end": v(-125, 505) * mm});
            skLineSegment(sketch, "E42.3.2.3", {"start": v(-225, 605) * mm, "end": v(-225, 505) * mm});
            skLineSegment(sketch, "E42.3.3.0", {"start": v(-225, 395) * mm, "end": v(-125, 395) * mm});
            skLineSegment(sketch, "E42.3.3.1", {"start": v(-225, 495) * mm, "end": v(-125, 495) * mm});
            skLineSegment(sketch, "E42.3.3.2", {"start": v(-125, 495) * mm, "end": v(-125, 395) * mm});
            skLineSegment(sketch, "E42.3.3.3", {"start": v(-225, 495) * mm, "end": v(-225, 395) * mm});
            skLineSegment(sketch, "E42.3.4.0", {"start": v(-225, 285) * mm, "end": v(-125, 285) * mm});
            skLineSegment(sketch, "E42.3.4.1", {"start": v(-225, 385) * mm, "end": v(-125, 385) * mm});
            skLineSegment(sketch, "E42.3.4.2", {"start": v(-125, 385) * mm, "end": v(-125, 285) * mm});
            skLineSegment(sketch, "E42.3.4.3", {"start": v(-225, 385) * mm, "end": v(-225, 285) * mm});
            skLineSegment(sketch, "E42.3.5.0", {"start": v(-225, 175) * mm, "end": v(-125, 175) * mm});
            skLineSegment(sketch, "E42.3.5.1", {"start": v(-225, 275) * mm, "end": v(-125, 275) * mm});
            skLineSegment(sketch, "E42.3.5.2", {"start": v(-125, 275) * mm, "end": v(-125, 175) * mm});
            skLineSegment(sketch, "E42.3.5.3", {"start": v(-225, 275) * mm, "end": v(-225, 175) * mm});
            skLineSegment(sketch, "E42.3.6.0", {"start": v(-225, 65) * mm, "end": v(-125, 65) * mm});
            skLineSegment(sketch, "E42.3.6.1", {"start": v(-225, 165) * mm, "end": v(-125, 165) * mm});
            skLineSegment(sketch, "E42.3.6.2", {"start": v(-125, 165) * mm, "end": v(-125, 65) * mm});
            skLineSegment(sketch, "E42.3.6.3", {"start": v(-225, 165) * mm, "end": v(-225, 65) * mm});
            skLineSegment(sketch, "E42.4.0.0", {"start": v(-115, 725) * mm, "end": v(-15, 725) * mm});
            skLineSegment(sketch, "E42.4.0.1", {"start": v(-115, 825) * mm, "end": v(-15, 825) * mm});
            skLineSegment(sketch, "E42.4.0.2", {"start": v(-15, 825) * mm, "end": v(-15, 725) * mm});
            skLineSegment(sketch, "E42.4.0.3", {"start": v(-115, 825) * mm, "end": v(-115, 725) * mm});
            skLineSegment(sketch, "E42.4.1.0", {"start": v(-115, 615) * mm, "end": v(-15, 615) * mm});
            skLineSegment(sketch, "E42.4.1.1", {"start": v(-115, 715) * mm, "end": v(-15, 715) * mm});
            skLineSegment(sketch, "E42.4.1.2", {"start": v(-15, 715) * mm, "end": v(-15, 615) * mm});
            skLineSegment(sketch, "E42.4.1.3", {"start": v(-115, 715) * mm, "end": v(-115, 615) * mm});
            skLineSegment(sketch, "E42.4.2.0", {"start": v(-115, 505) * mm, "end": v(-15, 505) * mm});
            skLineSegment(sketch, "E42.4.2.1", {"start": v(-115, 605) * mm, "end": v(-15, 605) * mm});
            skLineSegment(sketch, "E42.4.2.2", {"start": v(-15, 605) * mm, "end": v(-15, 505) * mm});
            skLineSegment(sketch, "E42.4.2.3", {"start": v(-115, 605) * mm, "end": v(-115, 505) * mm});
            skLineSegment(sketch, "E42.4.3.0", {"start": v(-115, 395) * mm, "end": v(-15, 395) * mm});
            skLineSegment(sketch, "E42.4.3.1", {"start": v(-115, 495) * mm, "end": v(-15, 495) * mm});
            skLineSegment(sketch, "E42.4.3.2", {"start": v(-15, 495) * mm, "end": v(-15, 395) * mm});
            skLineSegment(sketch, "E42.4.3.3", {"start": v(-115, 495) * mm, "end": v(-115, 395) * mm});
            skLineSegment(sketch, "E42.4.4.0", {"start": v(-115, 285) * mm, "end": v(-15, 285) * mm});
            skLineSegment(sketch, "E42.4.4.1", {"start": v(-115, 385) * mm, "end": v(-15, 385) * mm});
            skLineSegment(sketch, "E42.4.4.2", {"start": v(-15, 385) * mm, "end": v(-15, 285) * mm});
            skLineSegment(sketch, "E42.4.4.3", {"start": v(-115, 385) * mm, "end": v(-115, 285) * mm});
            skLineSegment(sketch, "E42.4.5.0", {"start": v(-115, 175) * mm, "end": v(-15, 175) * mm});
            skLineSegment(sketch, "E42.4.5.1", {"start": v(-115, 275) * mm, "end": v(-15, 275) * mm});
            skLineSegment(sketch, "E42.4.5.2", {"start": v(-15, 275) * mm, "end": v(-15, 175) * mm});
            skLineSegment(sketch, "E42.4.5.3", {"start": v(-115, 275) * mm, "end": v(-115, 175) * mm});
            skLineSegment(sketch, "E42.4.6.0", {"start": v(-115, 65) * mm, "end": v(-15, 65) * mm});
            skLineSegment(sketch, "E42.4.6.1", {"start": v(-115, 165) * mm, "end": v(-15, 165) * mm});
            skLineSegment(sketch, "E42.4.6.2", {"start": v(-15, 165) * mm, "end": v(-15, 65) * mm});
            skLineSegment(sketch, "E42.4.6.3", {"start": v(-115, 165) * mm, "end": v(-115, 65) * mm});
            skLineSegment(sketch, "E42.5.0.0", {"start": v(-5, 725) * mm, "end": v(95, 725) * mm});
            skLineSegment(sketch, "E42.5.0.1", {"start": v(-5, 825) * mm, "end": v(95, 825) * mm});
            skLineSegment(sketch, "E42.5.0.2", {"start": v(95, 825) * mm, "end": v(95, 725) * mm});
            skLineSegment(sketch, "E42.5.0.3", {"start": v(-5, 825) * mm, "end": v(-5, 725) * mm});
            skLineSegment(sketch, "E42.5.1.0", {"start": v(-5, 615) * mm, "end": v(95, 615) * mm});
            skLineSegment(sketch, "E42.5.1.1", {"start": v(-5, 715) * mm, "end": v(95, 715) * mm});
            skLineSegment(sketch, "E42.5.1.2", {"start": v(95, 715) * mm, "end": v(95, 615) * mm});
            skLineSegment(sketch, "E42.5.1.3", {"start": v(-5, 715) * mm, "end": v(-5, 615) * mm});
            skLineSegment(sketch, "E42.5.2.0", {"start": v(-5, 505) * mm, "end": v(95, 505) * mm});
            skLineSegment(sketch, "E42.5.2.1", {"start": v(-5, 605) * mm, "end": v(95, 605) * mm});
            skLineSegment(sketch, "E42.5.2.2", {"start": v(95, 605) * mm, "end": v(95, 505) * mm});
            skLineSegment(sketch, "E42.5.2.3", {"start": v(-5, 605) * mm, "end": v(-5, 505) * mm});
            skLineSegment(sketch, "E42.5.3.0", {"start": v(-5, 395) * mm, "end": v(95, 395) * mm});
            skLineSegment(sketch, "E42.5.3.1", {"start": v(-5, 495) * mm, "end": v(95, 495) * mm});
            skLineSegment(sketch, "E42.5.3.2", {"start": v(95, 495) * mm, "end": v(95, 395) * mm});
            skLineSegment(sketch, "E42.5.3.3", {"start": v(-5, 495) * mm, "end": v(-5, 395) * mm});
            skLineSegment(sketch, "E42.5.4.0", {"start": v(-5, 285) * mm, "end": v(95, 285) * mm});
            skLineSegment(sketch, "E42.5.4.1", {"start": v(-5, 385) * mm, "end": v(95, 385) * mm});
            skLineSegment(sketch, "E42.5.4.2", {"start": v(95, 385) * mm, "end": v(95, 285) * mm});
            skLineSegment(sketch, "E42.5.4.3", {"start": v(-5, 385) * mm, "end": v(-5, 285) * mm});
            skLineSegment(sketch, "E42.5.5.0", {"start": v(-5, 175) * mm, "end": v(95, 175) * mm});
            skLineSegment(sketch, "E42.5.5.1", {"start": v(-5, 275) * mm, "end": v(95, 275) * mm});
            skLineSegment(sketch, "E42.5.5.2", {"start": v(95, 275) * mm, "end": v(95, 175) * mm});
            skLineSegment(sketch, "E42.5.5.3", {"start": v(-5, 275) * mm, "end": v(-5, 175) * mm});
            skLineSegment(sketch, "E42.5.6.0", {"start": v(-5, 65) * mm, "end": v(95, 65) * mm});
            skLineSegment(sketch, "E42.5.6.1", {"start": v(-5, 165) * mm, "end": v(95, 165) * mm});
            skLineSegment(sketch, "E42.5.6.2", {"start": v(95, 165) * mm, "end": v(95, 65) * mm});
            skLineSegment(sketch, "E42.5.6.3", {"start": v(-5, 165) * mm, "end": v(-5, 65) * mm});
            skLineSegment(sketch, "E42.6.0.0", {"start": v(105, 725) * mm, "end": v(205, 725) * mm});
            skLineSegment(sketch, "E42.6.0.1", {"start": v(105, 825) * mm, "end": v(205, 825) * mm});
            skLineSegment(sketch, "E42.6.0.2", {"start": v(205, 825) * mm, "end": v(205, 725) * mm});
            skLineSegment(sketch, "E42.6.0.3", {"start": v(105, 825) * mm, "end": v(105, 725) * mm});
            skLineSegment(sketch, "E42.6.1.0", {"start": v(105, 615) * mm, "end": v(205, 615) * mm});
            skLineSegment(sketch, "E42.6.1.1", {"start": v(105, 715) * mm, "end": v(205, 715) * mm});
            skLineSegment(sketch, "E42.6.1.2", {"start": v(205, 715) * mm, "end": v(205, 615) * mm});
            skLineSegment(sketch, "E42.6.1.3", {"start": v(105, 715) * mm, "end": v(105, 615) * mm});
            skLineSegment(sketch, "E42.6.2.0", {"start": v(105, 505) * mm, "end": v(205, 505) * mm});
            skLineSegment(sketch, "E42.6.2.1", {"start": v(105, 605) * mm, "end": v(205, 605) * mm});
            skLineSegment(sketch, "E42.6.2.2", {"start": v(205, 605) * mm, "end": v(205, 505) * mm});
            skLineSegment(sketch, "E42.6.2.3", {"start": v(105, 605) * mm, "end": v(105, 505) * mm});
            skLineSegment(sketch, "E42.6.3.0", {"start": v(105, 395) * mm, "end": v(205, 395) * mm});
            skLineSegment(sketch, "E42.6.3.1", {"start": v(105, 495) * mm, "end": v(205, 495) * mm});
            skLineSegment(sketch, "E42.6.3.2", {"start": v(205, 495) * mm, "end": v(205, 395) * mm});
            skLineSegment(sketch, "E42.6.3.3", {"start": v(105, 495) * mm, "end": v(105, 395) * mm});
            skLineSegment(sketch, "E42.6.4.0", {"start": v(105, 285) * mm, "end": v(205, 285) * mm});
            skLineSegment(sketch, "E42.6.4.1", {"start": v(105, 385) * mm, "end": v(205, 385) * mm});
            skLineSegment(sketch, "E42.6.4.2", {"start": v(205, 385) * mm, "end": v(205, 285) * mm});
            skLineSegment(sketch, "E42.6.4.3", {"start": v(105, 385) * mm, "end": v(105, 285) * mm});
            skLineSegment(sketch, "E42.6.5.0", {"start": v(105, 175) * mm, "end": v(205, 175) * mm});
            skLineSegment(sketch, "E42.6.5.1", {"start": v(105, 275) * mm, "end": v(205, 275) * mm});
            skLineSegment(sketch, "E42.6.5.2", {"start": v(205, 275) * mm, "end": v(205, 175) * mm});
            skLineSegment(sketch, "E42.6.5.3", {"start": v(105, 275) * mm, "end": v(105, 175) * mm});
            skLineSegment(sketch, "E42.6.6.0", {"start": v(105, 65) * mm, "end": v(205, 65) * mm});
            skLineSegment(sketch, "E42.6.6.1", {"start": v(105, 165) * mm, "end": v(205, 165) * mm});
            skLineSegment(sketch, "E42.6.6.2", {"start": v(205, 165) * mm, "end": v(205, 65) * mm});
            skLineSegment(sketch, "E42.6.6.3", {"start": v(105, 165) * mm, "end": v(105, 65) * mm});
            skLineSegment(sketch, "E42.7.0.0", {"start": v(215, 725) * mm, "end": v(315, 725) * mm});
            skLineSegment(sketch, "E42.7.0.1", {"start": v(215, 825) * mm, "end": v(315, 825) * mm});
            skLineSegment(sketch, "E42.7.0.2", {"start": v(315, 825) * mm, "end": v(315, 725) * mm});
            skLineSegment(sketch, "E42.7.0.3", {"start": v(215, 825) * mm, "end": v(215, 725) * mm});
            skLineSegment(sketch, "E42.7.1.0", {"start": v(215, 615) * mm, "end": v(315, 615) * mm});
            skLineSegment(sketch, "E42.7.1.1", {"start": v(215, 715) * mm, "end": v(315, 715) * mm});
            skLineSegment(sketch, "E42.7.1.2", {"start": v(315, 715) * mm, "end": v(315, 615) * mm});
            skLineSegment(sketch, "E42.7.1.3", {"start": v(215, 715) * mm, "end": v(215, 615) * mm});
            skLineSegment(sketch, "E42.7.2.0", {"start": v(215, 505) * mm, "end": v(315, 505) * mm});
            skLineSegment(sketch, "E42.7.2.1", {"start": v(215, 605) * mm, "end": v(315, 605) * mm});
            skLineSegment(sketch, "E42.7.2.2", {"start": v(315, 605) * mm, "end": v(315, 505) * mm});
            skLineSegment(sketch, "E42.7.2.3", {"start": v(215, 605) * mm, "end": v(215, 505) * mm});
            skLineSegment(sketch, "E42.7.3.0", {"start": v(215, 395) * mm, "end": v(315, 395) * mm});
            skLineSegment(sketch, "E42.7.3.1", {"start": v(215, 495) * mm, "end": v(315, 495) * mm});
            skLineSegment(sketch, "E42.7.3.2", {"start": v(315, 495) * mm, "end": v(315, 395) * mm});
            skLineSegment(sketch, "E42.7.3.3", {"start": v(215, 495) * mm, "end": v(215, 395) * mm});
            skLineSegment(sketch, "E42.7.4.0", {"start": v(215, 285) * mm, "end": v(315, 285) * mm});
            skLineSegment(sketch, "E42.7.4.1", {"start": v(215, 385) * mm, "end": v(315, 385) * mm});
            skLineSegment(sketch, "E42.7.4.2", {"start": v(315, 385) * mm, "end": v(315, 285) * mm});
            skLineSegment(sketch, "E42.7.4.3", {"start": v(215, 385) * mm, "end": v(215, 285) * mm});
            skLineSegment(sketch, "E42.7.5.0", {"start": v(215, 175) * mm, "end": v(315, 175) * mm});
            skLineSegment(sketch, "E42.7.5.1", {"start": v(215, 275) * mm, "end": v(315, 275) * mm});
            skLineSegment(sketch, "E42.7.5.2", {"start": v(315, 275) * mm, "end": v(315, 175) * mm});
            skLineSegment(sketch, "E42.7.5.3", {"start": v(215, 275) * mm, "end": v(215, 175) * mm});
            skLineSegment(sketch, "E42.7.6.0", {"start": v(215, 65) * mm, "end": v(315, 65) * mm});
            skLineSegment(sketch, "E42.7.6.1", {"start": v(215, 165) * mm, "end": v(315, 165) * mm});
            skLineSegment(sketch, "E42.7.6.2", {"start": v(315, 165) * mm, "end": v(315, 65) * mm});
            skLineSegment(sketch, "E42.7.6.3", {"start": v(215, 165) * mm, "end": v(215, 65) * mm});
            skLineSegment(sketch, "E42.8.0.0", {"start": v(325, 725) * mm, "end": v(425, 725) * mm});
            skLineSegment(sketch, "E42.8.0.1", {"start": v(325, 825) * mm, "end": v(425, 825) * mm});
            skLineSegment(sketch, "E42.8.0.2", {"start": v(425, 825) * mm, "end": v(425, 725) * mm});
            skLineSegment(sketch, "E42.8.0.3", {"start": v(325, 825) * mm, "end": v(325, 725) * mm});
            skLineSegment(sketch, "E42.8.1.0", {"start": v(325, 615) * mm, "end": v(425, 615) * mm});
            skLineSegment(sketch, "E42.8.1.1", {"start": v(325, 715) * mm, "end": v(425, 715) * mm});
            skLineSegment(sketch, "E42.8.1.2", {"start": v(425, 715) * mm, "end": v(425, 615) * mm});
            skLineSegment(sketch, "E42.8.1.3", {"start": v(325, 715) * mm, "end": v(325, 615) * mm});
            skLineSegment(sketch, "E42.8.2.0", {"start": v(325, 505) * mm, "end": v(425, 505) * mm});
            skLineSegment(sketch, "E42.8.2.1", {"start": v(325, 605) * mm, "end": v(425, 605) * mm});
            skLineSegment(sketch, "E42.8.2.2", {"start": v(425, 605) * mm, "end": v(425, 505) * mm});
            skLineSegment(sketch, "E42.8.2.3", {"start": v(325, 605) * mm, "end": v(325, 505) * mm});
            skLineSegment(sketch, "E42.8.3.0", {"start": v(325, 395) * mm, "end": v(425, 395) * mm});
            skLineSegment(sketch, "E42.8.3.1", {"start": v(325, 495) * mm, "end": v(425, 495) * mm});
            skLineSegment(sketch, "E42.8.3.2", {"start": v(425, 495) * mm, "end": v(425, 395) * mm});
            skLineSegment(sketch, "E42.8.3.3", {"start": v(325, 495) * mm, "end": v(325, 395) * mm});
            skLineSegment(sketch, "E42.8.4.0", {"start": v(325, 285) * mm, "end": v(425, 285) * mm});
            skLineSegment(sketch, "E42.8.4.1", {"start": v(325, 385) * mm, "end": v(425, 385) * mm});
            skLineSegment(sketch, "E42.8.4.2", {"start": v(425, 385) * mm, "end": v(425, 285) * mm});
            skLineSegment(sketch, "E42.8.4.3", {"start": v(325, 385) * mm, "end": v(325, 285) * mm});
            skLineSegment(sketch, "E42.8.5.0", {"start": v(325, 175) * mm, "end": v(425, 175) * mm});
            skLineSegment(sketch, "E42.8.5.1", {"start": v(325, 275) * mm, "end": v(425, 275) * mm});
            skLineSegment(sketch, "E42.8.5.2", {"start": v(425, 275) * mm, "end": v(425, 175) * mm});
            skLineSegment(sketch, "E42.8.5.3", {"start": v(325, 275) * mm, "end": v(325, 175) * mm});
            skLineSegment(sketch, "E42.8.6.0", {"start": v(325, 65) * mm, "end": v(425, 65) * mm});
            skLineSegment(sketch, "E42.8.6.1", {"start": v(325, 165) * mm, "end": v(425, 165) * mm});
            skLineSegment(sketch, "E42.8.6.2", {"start": v(425, 165) * mm, "end": v(425, 65) * mm});
            skLineSegment(sketch, "E42.8.6.3", {"start": v(325, 165) * mm, "end": v(325, 65) * mm});
            skLineSegment(sketch, "E42.9.0.0", {"start": v(435, 725) * mm, "end": v(535, 725) * mm});
            skLineSegment(sketch, "E42.9.0.1", {"start": v(435, 825) * mm, "end": v(535, 825) * mm});
            skLineSegment(sketch, "E42.9.0.2", {"start": v(535, 825) * mm, "end": v(535, 725) * mm});
            skLineSegment(sketch, "E42.9.0.3", {"start": v(435, 825) * mm, "end": v(435, 725) * mm});
            skLineSegment(sketch, "E42.9.1.0", {"start": v(435, 615) * mm, "end": v(535, 615) * mm});
            skLineSegment(sketch, "E42.9.1.1", {"start": v(435, 715) * mm, "end": v(535, 715) * mm});
            skLineSegment(sketch, "E42.9.1.2", {"start": v(535, 715) * mm, "end": v(535, 615) * mm});
            skLineSegment(sketch, "E42.9.1.3", {"start": v(435, 715) * mm, "end": v(435, 615) * mm});
            skLineSegment(sketch, "E42.9.2.0", {"start": v(435, 505) * mm, "end": v(535, 505) * mm});
            skLineSegment(sketch, "E42.9.2.1", {"start": v(435, 605) * mm, "end": v(535, 605) * mm});
            skLineSegment(sketch, "E42.9.2.2", {"start": v(535, 605) * mm, "end": v(535, 505) * mm});
            skLineSegment(sketch, "E42.9.2.3", {"start": v(435, 605) * mm, "end": v(435, 505) * mm});
            skLineSegment(sketch, "E42.9.3.0", {"start": v(435, 395) * mm, "end": v(535, 395) * mm});
            skLineSegment(sketch, "E42.9.3.1", {"start": v(435, 495) * mm, "end": v(535, 495) * mm});
            skLineSegment(sketch, "E42.9.3.2", {"start": v(535, 495) * mm, "end": v(535, 395) * mm});
            skLineSegment(sketch, "E42.9.3.3", {"start": v(435, 495) * mm, "end": v(435, 395) * mm});
            skLineSegment(sketch, "E42.9.4.0", {"start": v(435, 285) * mm, "end": v(535, 285) * mm});
            skLineSegment(sketch, "E42.9.4.1", {"start": v(435, 385) * mm, "end": v(535, 385) * mm});
            skLineSegment(sketch, "E42.9.4.2", {"start": v(535, 385) * mm, "end": v(535, 285) * mm});
            skLineSegment(sketch, "E42.9.4.3", {"start": v(435, 385) * mm, "end": v(435, 285) * mm});
            skLineSegment(sketch, "E42.9.5.0", {"start": v(435, 175) * mm, "end": v(535, 175) * mm});
            skLineSegment(sketch, "E42.9.5.1", {"start": v(435, 275) * mm, "end": v(535, 275) * mm});
            skLineSegment(sketch, "E42.9.5.2", {"start": v(535, 275) * mm, "end": v(535, 175) * mm});
            skLineSegment(sketch, "E42.9.5.3", {"start": v(435, 275) * mm, "end": v(435, 175) * mm});
            skLineSegment(sketch, "E42.9.6.0", {"start": v(435, 65) * mm, "end": v(535, 65) * mm});
            skLineSegment(sketch, "E42.9.6.1", {"start": v(435, 165) * mm, "end": v(535, 165) * mm});
            skLineSegment(sketch, "E42.9.6.2", {"start": v(535, 165) * mm, "end": v(535, 65) * mm});
            skLineSegment(sketch, "E42.9.6.3", {"start": v(435, 165) * mm, "end": v(435, 65) * mm});
            skLineSegment(sketch, "E42.direction1", {"start": v(-555, 725) * mm, "end": v(-445, 725) * mm, "construction": true});
            skLineSegment(sketch, "E42.direction2", {"start": v(-555, 725) * mm, "end": v(-555, 615) * mm, "construction": true});
            skSolve(sketch);
        }
        {
            var Q0;
            Q0 = qSketchRegion(id + "F11", true);
            extrude(context, id + "F12", {"entities" : qUnion([Q0]), "operationType" : NewBodyOperationType.REMOVE, "endBound" : BoundingType.THROUGH_ALL, "oppositeDirection" : true, "depth" : 25 * mm});
        }
    });
